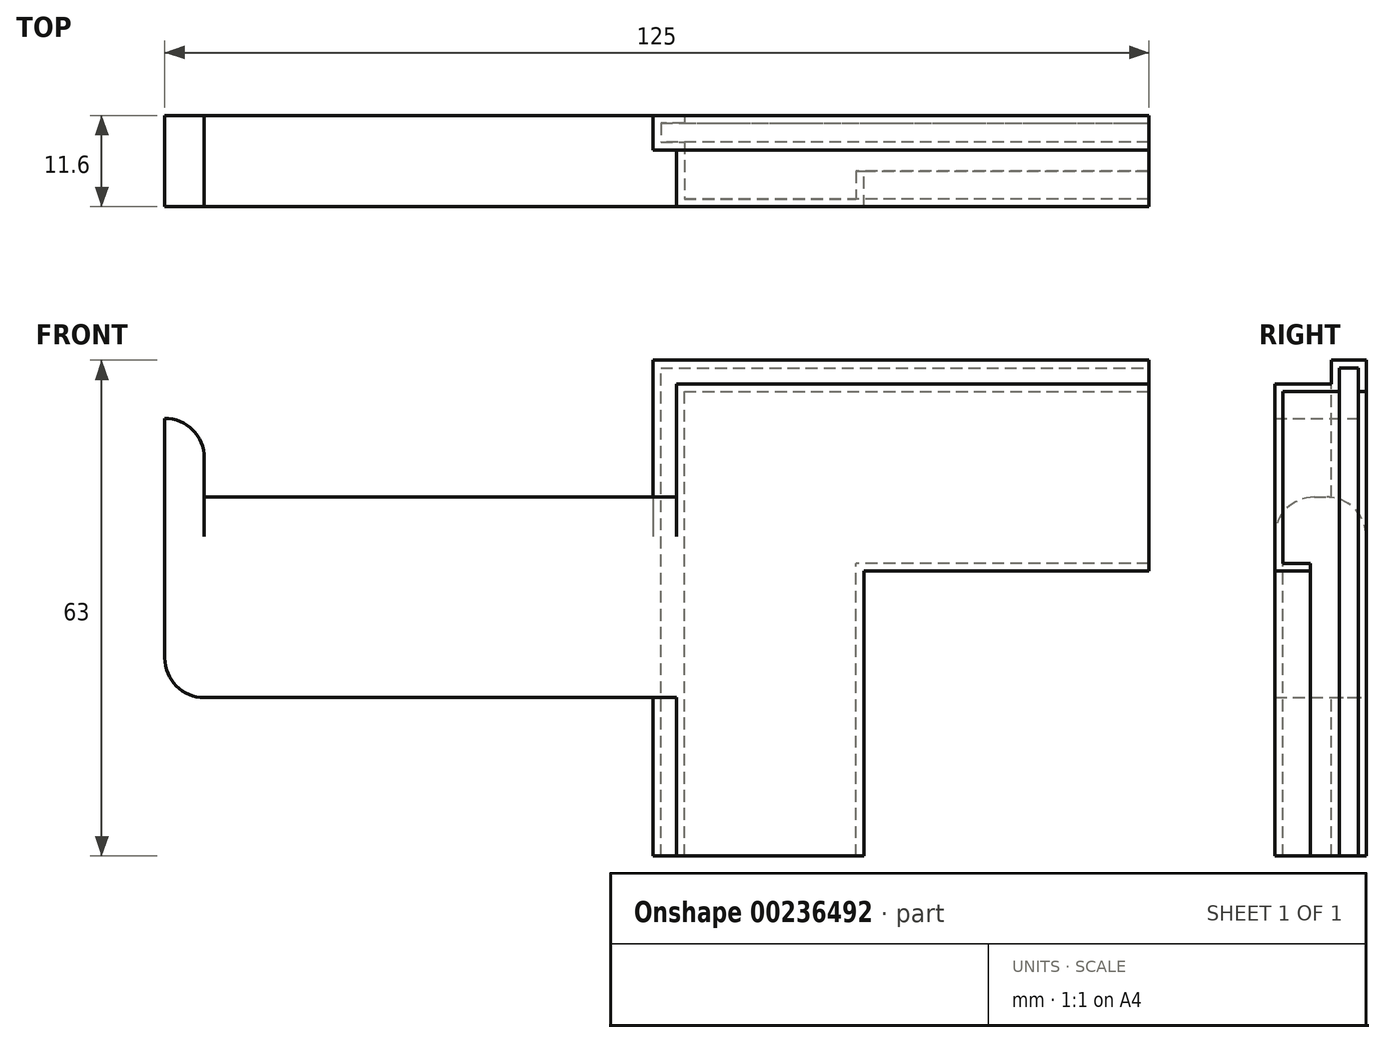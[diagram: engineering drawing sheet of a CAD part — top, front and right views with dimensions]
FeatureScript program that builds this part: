
annotation { "Feature Type Name" : "Feature", "Feature Type Description" : "" }
export const myFeature = defineFeature(function(context is Context, id is Id, definition is map)
    precondition{}
    {
        {
            var Q0;
            Q0=qCreatedBy(makeId("Front.planeOp"),FACE);
            var sketch = newSketch(context, id + "F0", { "sketchPlane" : qUnion([Q0])});
            skLineSegment(sketch, "E0.bottom", {"start": v(-30, 30) * mm, "end": v(30, 30) * mm});
            skLineSegment(sketch, "E0.top", {"start": v(-30, 6.2) * mm, "end": v(30, 6.2) * mm});
            skLineSegment(sketch, "E0.left", {"start": v(-30, 30) * mm, "end": v(-30, 6.2) * mm});
            skLineSegment(sketch, "E0.right", {"start": v(30, 30) * mm, "end": v(30, 6.2) * mm});
            skLineSegment(sketch, "E1.bottom", {"start": v(-30, 30) * mm, "end": v(-6.2, 30) * mm});
            skLineSegment(sketch, "E1.top", {"start": v(-30, -30) * mm, "end": v(-6.2, -30) * mm});
            skLineSegment(sketch, "E1.left", {"start": v(-30, 30) * mm, "end": v(-30, -30) * mm});
            skLineSegment(sketch, "E1.right", {"start": v(-6.2, 30) * mm, "end": v(-6.2, -30) * mm});
            skSolve(sketch);
        }
        {
            var Q0;
            Q0 = qSketchRegion(id + "F0", true);
            extrude(context, id + "F1", {"entities" : qUnion([Q0]), "depth" : 1 * mm});
        }
        {
            var Q0;
            Q0=makeQuery(id+"F1.opExtrude","CAP_FACE",FACE,{"disambiguationData":[OSD([sQuery(id+"F0.wireOp",EDGE,"E0.bottom"),sQuery(id+"F0.wireOp",EDGE,"E0.top"),sQuery(id+"F0.wireOp",EDGE,"E0.right"),sQuery(id+"F0.wireOp",EDGE,"E1.bottom"),sQuery(id+"F0.wireOp",EDGE,"E1.top"),sQuery(id+"F0.wireOp",EDGE,"E1.left"),sQuery(id+"F0.wireOp",EDGE,"E1.right")])],"isStart":true});
            var sketch = newSketch(context, id + "F2", { "sketchPlane" : qUnion([Q0])});
            skLineSegment(sketch, "E2.bottom", {"start": v(-30, 30) * mm, "end": v(30, 30) * mm});
            skLineSegment(sketch, "E2.top", {"start": v(-30, 29) * mm, "end": v(30, 29) * mm});
            skLineSegment(sketch, "E2.left", {"start": v(-30, 30) * mm, "end": v(-30, 29) * mm});
            skLineSegment(sketch, "E2.right", {"start": v(30, 30) * mm, "end": v(30, 29) * mm});
            skLineSegment(sketch, "E3.bottom", {"start": v(30, 30) * mm, "end": v(29, 30) * mm});
            skLineSegment(sketch, "E3.top", {"start": v(30, -30) * mm, "end": v(29, -30) * mm});
            skLineSegment(sketch, "E3.left", {"start": v(30, 30) * mm, "end": v(30, -30) * mm});
            skLineSegment(sketch, "E3.right", {"start": v(29, 30) * mm, "end": v(29, -30) * mm});
            skSolve(sketch);
        }
        {
            var Q0;
            Q0 = qSketchRegion(id + "F2", true);
            extrude(context, id + "F3", {"entities" : qUnion([Q0]), "operationType" : NewBodyOperationType.ADD, "depth" : 7.2 * mm});
        }
        {
            var Q0;
            Q0=makeQuery(id+"F1.opExtrude","CAP_FACE",FACE,{"disambiguationData":[OSD([sQuery(id+"F0.wireOp",EDGE,"E0.bottom"),sQuery(id+"F0.wireOp",EDGE,"E0.top"),sQuery(id+"F0.wireOp",EDGE,"E0.right"),sQuery(id+"F0.wireOp",EDGE,"E1.bottom"),sQuery(id+"F0.wireOp",EDGE,"E1.top"),sQuery(id+"F0.wireOp",EDGE,"E1.left"),sQuery(id+"F0.wireOp",EDGE,"E1.right")])],"isStart":true});
            var sketch = newSketch(context, id + "F4", { "sketchPlane" : qUnion([Q0])});
            skLineSegment(sketch, "E4.bottom", {"start": v(-30, 6.2) * mm, "end": v(6.2, 6.2) * mm});
            skLineSegment(sketch, "E4.top", {"start": v(-30, 7.2) * mm, "end": v(6.2, 7.2) * mm});
            skLineSegment(sketch, "E4.left", {"start": v(-30, 6.2) * mm, "end": v(-30, 7.2) * mm});
            skLineSegment(sketch, "E4.right", {"start": v(6.2, 6.2) * mm, "end": v(6.2, 7.2) * mm});
            skLineSegment(sketch, "E5.bottom", {"start": v(6.2, -30) * mm, "end": v(7.2, -30) * mm});
            skLineSegment(sketch, "E5.top", {"start": v(6.2, 7.2) * mm, "end": v(7.2, 7.2) * mm});
            skLineSegment(sketch, "E5.left", {"start": v(6.2, -30) * mm, "end": v(6.2, 7.2) * mm});
            skLineSegment(sketch, "E5.right", {"start": v(7.2, -30) * mm, "end": v(7.2, 7.2) * mm});
            skSolve(sketch);
        }
        {
            var Q0;
            Q0 = qSketchRegion(id + "F4", true);
            extrude(context, id + "F5", {"entities" : qUnion([Q0]), "operationType" : NewBodyOperationType.ADD, "depth" : 3.5 * mm});
        }
        {
            var Q0;
            Q0=makeQuery(id+"F3.boolean.opBoolean","MERGE",FACE,{"derivedFrom":[makeQuery(id+"F1.opExtrude","SWEPT_FACE",FACE,{"disambiguationData":[OSD([sQuery(id+"F0.wireOp",EDGE,"E0.bottom"),sQuery(id+"F0.wireOp",EDGE,"E1.bottom")])]}),makeQuery(id+"F3.opExtrude","SWEPT_FACE",FACE,{"disambiguationData":[OSD([sQuery(id+"F2.wireOp",EDGE,"E2.bottom"),sQuery(id+"F2.wireOp",EDGE,"E3.bottom")])]})]});
            var sketch = newSketch(context, id + "F6", { "sketchPlane" : qUnion([Q0])});
            skLineSegment(sketch, "E6.bottom", {"start": v(-30, 7.2) * mm, "end": v(30, 7.2) * mm});
            skLineSegment(sketch, "E6.top", {"start": v(-30, 6.2) * mm, "end": v(30, 6.2) * mm});
            skLineSegment(sketch, "E6.left", {"start": v(-30, 7.2) * mm, "end": v(-30, 6.2) * mm});
            skLineSegment(sketch, "E6.right", {"start": v(30, 7.2) * mm, "end": v(30, 6.2) * mm});
            skSolve(sketch);
        }
        {
            var Q0;
            Q0 = qSketchRegion(id + "F6", true);
            extrude(context, id + "F7", {"entities" : qUnion([Q0]), "operationType" : NewBodyOperationType.ADD, "depth" : 3 * mm});
        }
        {
            var Q0;
            Q0=makeQuery(id+"F7.boolean.opBoolean","MERGE",FACE,{"derivedFrom":[makeQuery(id+"F3.opExtrude","CAP_FACE",FACE,{"disambiguationData":[OSD([sQuery(id+"F2.wireOp",EDGE,"E2.bottom"),sQuery(id+"F2.wireOp",EDGE,"E2.top"),sQuery(id+"F2.wireOp",EDGE,"E2.left"),sQuery(id+"F2.wireOp",EDGE,"E3.bottom"),sQuery(id+"F2.wireOp",EDGE,"E3.top"),sQuery(id+"F2.wireOp",EDGE,"E3.left"),sQuery(id+"F2.wireOp",EDGE,"E3.right")])],"isStart":false}),makeQuery(id+"F7.opExtrude","SWEPT_FACE",FACE,{"disambiguationData":[OSD([sQuery(id+"F6.wireOp",EDGE,"E6.bottom")])]})]});
            var sketch = newSketch(context, id + "F8", { "sketchPlane" : qUnion([Q0])});
            skLineSegment(sketch, "E7.bottom", {"start": v(-30, 33) * mm, "end": v(30, 33) * mm});
            skLineSegment(sketch, "E7.top", {"start": v(-30, 32) * mm, "end": v(30, 32) * mm});
            skLineSegment(sketch, "E7.left", {"start": v(-30, 33) * mm, "end": v(-30, 32) * mm});
            skLineSegment(sketch, "E7.right", {"start": v(30, 33) * mm, "end": v(30, 32) * mm});
            skSolve(sketch);
        }
        {
            var Q0;
            Q0 = qSketchRegion(id + "F8", true);
            extrude(context, id + "F9", {"entities" : qUnion([Q0]), "operationType" : NewBodyOperationType.ADD, "depth" : 3.4 * mm});
        }
        {
            var Q0;
            Q0=makeQuery(id+"F9.opExtrude","SWEPT_FACE",FACE,{"disambiguationData":[OSD([sQuery(id+"F8.wireOp",EDGE,"E7.top")])]});
            var sketch = newSketch(context, id + "F10", { "sketchPlane" : qUnion([Q0])});
            skLineSegment(sketch, "E8.bottom", {"start": v(-30, -10.6) * mm, "end": v(30, -10.6) * mm});
            skLineSegment(sketch, "E8.top", {"start": v(-30, -9.6) * mm, "end": v(30, -9.6) * mm});
            skLineSegment(sketch, "E8.left", {"start": v(-30, -10.6) * mm, "end": v(-30, -9.6) * mm});
            skLineSegment(sketch, "E8.right", {"start": v(30, -10.6) * mm, "end": v(30, -9.6) * mm});
            skSolve(sketch);
        }
        {
            var Q0;
            Q0 = qSketchRegion(id + "F10", true);
            extrude(context, id + "F11", {"entities" : qUnion([Q0]), "operationType" : NewBodyOperationType.ADD, "depth" : 3 * mm});
        }
        {
            var Q0;
            Q0=makeQuery(id+"F11.boolean.opBoolean","MERGE",FACE,{"derivedFrom":[makeQuery(id+"F9.boolean.opBoolean","MERGE",FACE,{"derivedFrom":[makeQuery(id+"F7.boolean.opBoolean","MERGE",FACE,{"derivedFrom":[makeQuery(id+"F3.boolean.opBoolean","MERGE",FACE,{"derivedFrom":[makeQuery(id+"F1.opExtrude","SWEPT_FACE",FACE,{"disambiguationData":[OSD([sQuery(id+"F0.wireOp",EDGE,"E1.left")])]}),makeQuery(id+"F3.opExtrude","SWEPT_FACE",FACE,{"disambiguationData":[OSD([sQuery(id+"F2.wireOp",EDGE,"E3.left")])]})]}),makeQuery(id+"F7.opExtrude","SWEPT_FACE",FACE,{"disambiguationData":[OSD([sQuery(id+"F6.wireOp",EDGE,"E6.left")])]})]}),makeQuery(id+"F9.opExtrude","SWEPT_FACE",FACE,{"disambiguationData":[OSD([sQuery(id+"F8.wireOp",EDGE,"E7.right")])]})]}),makeQuery(id+"F11.opExtrude","SWEPT_FACE",FACE,{"disambiguationData":[OSD([sQuery(id+"F10.wireOp",EDGE,"E8.left")])]})]});
            var sketch = newSketch(context, id + "F12", { "sketchPlane" : qUnion([Q0])});
            skLineSegment(sketch, "E9.bottom", {"start": v(-7.2, -30) * mm, "end": v(-6.2, -30) * mm});
            skLineSegment(sketch, "E9.top", {"start": v(-7.2, 30) * mm, "end": v(-6.2, 30) * mm});
            skLineSegment(sketch, "E9.left", {"start": v(-7.2, -30) * mm, "end": v(-7.2, 30) * mm});
            skLineSegment(sketch, "E9.right", {"start": v(-6.2, -30) * mm, "end": v(-6.2, 30) * mm});
            skSolve(sketch);
        }
        {
            var Q0;
            Q0 = qSketchRegion(id + "F12", true);
            extrude(context, id + "F13", {"entities" : qUnion([Q0]), "operationType" : NewBodyOperationType.ADD, "depth" : 3 * mm});
        }
        {
            var Q0;
            Q0=makeQuery(id+"F13.boolean.opBoolean","MERGE",FACE,{"derivedFrom":[makeQuery(id+"F7.boolean.opBoolean","MERGE",FACE,{"derivedFrom":[makeQuery(id+"F3.opExtrude","CAP_FACE",FACE,{"disambiguationData":[OSD([sQuery(id+"F2.wireOp",EDGE,"E2.bottom"),sQuery(id+"F2.wireOp",EDGE,"E2.top"),sQuery(id+"F2.wireOp",EDGE,"E2.left"),sQuery(id+"F2.wireOp",EDGE,"E3.bottom"),sQuery(id+"F2.wireOp",EDGE,"E3.top"),sQuery(id+"F2.wireOp",EDGE,"E3.left"),sQuery(id+"F2.wireOp",EDGE,"E3.right")])],"isStart":false}),makeQuery(id+"F7.opExtrude","SWEPT_FACE",FACE,{"disambiguationData":[OSD([sQuery(id+"F6.wireOp",EDGE,"E6.bottom")])]})]}),makeQuery(id+"F13.opExtrude","SWEPT_FACE",FACE,{"disambiguationData":[OSD([sQuery(id+"F12.wireOp",EDGE,"E9.left")])]})]});
            var sketch = newSketch(context, id + "F14", { "sketchPlane" : qUnion([Q0])});
            skLineSegment(sketch, "E10.bottom", {"start": v(33, -30) * mm, "end": v(32, -30) * mm});
            skLineSegment(sketch, "E10.top", {"start": v(33, 30) * mm, "end": v(32, 30) * mm});
            skLineSegment(sketch, "E10.left", {"start": v(33, -30) * mm, "end": v(33, 30) * mm});
            skLineSegment(sketch, "E10.right", {"start": v(32, -30) * mm, "end": v(32, 30) * mm});
            skSolve(sketch);
        }
        {
            var Q0;
            Q0 = qSketchRegion(id + "F14", true);
            extrude(context, id + "F15", {"entities" : qUnion([Q0]), "operationType" : NewBodyOperationType.ADD, "depth" : 3.4 * mm});
        }
        {
            var Q0;
            Q0=makeQuery(id+"F15.opExtrude","SWEPT_FACE",FACE,{"disambiguationData":[OSD([sQuery(id+"F14.wireOp",EDGE,"E10.right")])]});
            var sketch = newSketch(context, id + "F16", { "sketchPlane" : qUnion([Q0])});
            skLineSegment(sketch, "E11.bottom", {"start": v(10.6, -30) * mm, "end": v(9.6, -30) * mm});
            skLineSegment(sketch, "E11.top", {"start": v(10.6, 30) * mm, "end": v(9.6, 30) * mm});
            skLineSegment(sketch, "E11.left", {"start": v(10.6, -30) * mm, "end": v(10.6, 30) * mm});
            skLineSegment(sketch, "E11.right", {"start": v(9.6, -30) * mm, "end": v(9.6, 30) * mm});
            skSolve(sketch);
        }
        {
            var Q0;
            Q0 = qSketchRegion(id + "F16", true);
            extrude(context, id + "F17", {"entities" : qUnion([Q0]), "operationType" : NewBodyOperationType.ADD, "depth" : 3 * mm});
        }
        {
            var Q0;
            {var subQ1=sQuery(id+"F2.wireOp",EDGE,"E3.left");var subQ4=sQuery(id+"F6.wireOp",EDGE,"E6.left");var subQ5=sQuery(id+"F6.wireOp",EDGE,"E6.bottom");var subQ6=makeQuery(id+"F3.opExtrude","SWEPT_FACE",FACE,{"disambiguationData":[OSD([subQ1])]});var subQ7=sQuery(id+"F10.wireOp",EDGE,"E8.left");var subQ8=makeQuery(id+"F11.opExtrude","SWEPT_FACE",FACE,{"disambiguationData":[OSD([subQ7])]});var subQ9=makeQuery(id+"F1.opExtrude","SWEPT_FACE",FACE,{"disambiguationData":[OSD([sQuery(id+"F0.wireOp",EDGE,"E1.left")])]});var subQ12=makeQuery(id+"F7.opExtrude","SWEPT_FACE",FACE,{"disambiguationData":[OSD([subQ4])]});var subQ13=sQuery(id+"F8.wireOp",EDGE,"E7.right");var subQ14=makeQuery(id+"F9.opExtrude","SWEPT_FACE",FACE,{"disambiguationData":[OSD([subQ13])]});Q0=makeQuery(id+"F13.boolean.opBoolean","SPLIT",FACE,{"disambiguationData":[TD([makeQuery(id+"F7.opExtrude","SWEPT_FACE",FACE,{"disambiguationData":[OSD([subQ5])]})])],"derivedFrom":makeQuery(id+"F11.boolean.opBoolean","MERGE",FACE,{"derivedFrom":[makeQuery(id+"F9.boolean.opBoolean","MERGE",FACE,{"derivedFrom":[makeQuery(id+"F7.boolean.opBoolean","MERGE",FACE,{"derivedFrom":[makeQuery(id+"F3.boolean.opBoolean","MERGE",FACE,{"derivedFrom":[subQ9,subQ6]}),subQ12]}),subQ14]}),subQ8]})});}
            extrude(context, id + "F18", {"entities" : qUnion([Q0]), "operationType" : NewBodyOperationType.ADD, "depth" : 3 * mm});
        }
        {
            var Q0;
            Q0=makeQuery(id+"F17.boolean.opBoolean","MERGE",FACE,{"derivedFrom":[makeQuery(id+"F15.boolean.opBoolean","MERGE",FACE,{"derivedFrom":[makeQuery(id+"F13.opExtrude","SWEPT_FACE",FACE,{"disambiguationData":[OSD([sQuery(id+"F12.wireOp",EDGE,"E9.top")])]}),makeQuery(id+"F15.opExtrude","SWEPT_FACE",FACE,{"disambiguationData":[OSD([sQuery(id+"F14.wireOp",EDGE,"E10.top")])]})]}),makeQuery(id+"F17.opExtrude","SWEPT_FACE",FACE,{"disambiguationData":[OSD([sQuery(id+"F16.wireOp",EDGE,"E11.top")])]})]});
            extrude(context, id + "F19", {"entities" : qUnion([Q0]), "operationType" : NewBodyOperationType.ADD, "depth" : 2 * mm});
        }
        {
            var Q0;
            {var subQ2=makeQuery(id+"F3.opExtrude","SWEPT_FACE",FACE,{"disambiguationData":[OSD([sQuery(id+"F2.wireOp",EDGE,"E3.left")])]});var subQ3=sQuery(id+"F0.wireOp",EDGE,"E1.left");var subQ4=sQuery(id+"F0.wireOp",EDGE,"E1.top");var subQ5=makeQuery(id+"F11.opExtrude","SWEPT_FACE",FACE,{"disambiguationData":[OSD([sQuery(id+"F10.wireOp",EDGE,"E8.left")])]});var subQ6=makeQuery(id+"F7.opExtrude","SWEPT_FACE",FACE,{"disambiguationData":[OSD([sQuery(id+"F6.wireOp",EDGE,"E6.left")])]});var subQ7=makeQuery(id+"F9.opExtrude","SWEPT_FACE",FACE,{"disambiguationData":[OSD([sQuery(id+"F8.wireOp",EDGE,"E7.right")])]});var subQ8=makeQuery(id+"F1.opExtrude","SWEPT_FACE",FACE,{"disambiguationData":[OSD([subQ3])]});Q0=makeQuery(id+"F13.boolean.opBoolean","SPLIT",FACE,{"disambiguationData":[TD([makeQuery(id+"F1.opExtrude","SWEPT_FACE",FACE,{"disambiguationData":[OSD([subQ4])]})])],"derivedFrom":makeQuery(id+"F11.boolean.opBoolean","MERGE",FACE,{"derivedFrom":[makeQuery(id+"F9.boolean.opBoolean","MERGE",FACE,{"derivedFrom":[makeQuery(id+"F7.boolean.opBoolean","MERGE",FACE,{"derivedFrom":[makeQuery(id+"F3.boolean.opBoolean","MERGE",FACE,{"derivedFrom":[subQ8,subQ2]}),subQ6]}),subQ7]}),subQ5]})});}
            var sketch = newSketch(context, id + "F20", { "sketchPlane" : qUnion([Q0])});
            skLineSegment(sketch, "E12.bottom", {"start": v(1, 15.6) * mm, "end": v(-6.2, 15.6) * mm});
            skLineSegment(sketch, "E12.top", {"start": v(1, -9.85) * mm, "end": v(-6.2, -9.85) * mm});
            skLineSegment(sketch, "E12.left", {"start": v(1, 15.6) * mm, "end": v(1, -9.85) * mm});
            skLineSegment(sketch, "E12.right", {"start": v(-6.2, 15.6) * mm, "end": v(-6.2, -9.85) * mm});
            skSolve(sketch);
        }
        {
            var Q0;
            Q0 = qSketchRegion(id + "F20", true);
            extrude(context, id + "F21", {"entities" : qUnion([Q0]), "operationType" : NewBodyOperationType.ADD, "depth" : 65 * mm});
        }
        {
            var Q0;
            {var subQ0=sQuery(id+"F14.wireOp",EDGE,"E10.left");var subQ1=sQuery(id+"F12.wireOp",EDGE,"E9.top");Q0=makeQuery(id+"F19.boolean.opBoolean","MERGE",FACE,{"derivedFrom":[makeQuery(id+"F18.boolean.opBoolean","MERGE",FACE,{"derivedFrom":[makeQuery(id+"F15.boolean.opBoolean","MERGE",FACE,{"derivedFrom":[makeQuery(id+"F13.opExtrude","CAP_FACE",FACE,{"disambiguationData":[OSD([sQuery(id+"F12.wireOp",EDGE,"E9.bottom"),subQ1,sQuery(id+"F12.wireOp",EDGE,"E9.left"),sQuery(id+"F12.wireOp",EDGE,"E9.right")])],"isStart":false}),makeQuery(id+"F15.opExtrude","SWEPT_FACE",FACE,{"disambiguationData":[OSD([subQ0])]})]}),makeQuery(id+"F18.opExtrude","CAP_FACE",FACE,{"disambiguationData":[OSD([sQuery(id+"F0.wireOp",EDGE,"E1.left"),sQuery(id+"F2.wireOp",EDGE,"E3.left"),sQuery(id+"F6.wireOp",EDGE,"E6.left"),sQuery(id+"F8.wireOp",EDGE,"E7.right"),sQuery(id+"F10.wireOp",EDGE,"E8.left")])],"isStart":false})]}),makeQuery(id+"F19.opExtrude","SWEPT_FACE",FACE,{"disambiguationData":[OSD([subQ1,sQuery(id+"F14.wireOp",EDGE,"E10.top"),subQ0])]})]});}
            var sketch = newSketch(context, id + "F22", { "sketchPlane" : qUnion([Q0])});
            skLineSegment(sketch, "E13.bottom", {"start": v(-6.2, 15.6) * mm, "end": v(-10.6, 15.6) * mm});
            skLineSegment(sketch, "E13.top", {"start": v(-6.2, -9.85) * mm, "end": v(-10.6, -9.85) * mm});
            skLineSegment(sketch, "E13.left", {"start": v(-6.2, 15.6) * mm, "end": v(-6.2, -9.85) * mm});
            skLineSegment(sketch, "E13.right", {"start": v(-10.6, 15.6) * mm, "end": v(-10.6, -9.85) * mm});
            skSolve(sketch);
        }
        {
            var Q0;
            Q0 = qSketchRegion(id + "F22", true);
            extrude(context, id + "F23", {"entities" : qUnion([Q0]), "operationType" : NewBodyOperationType.ADD, "depth" : 62 * mm});
        }
        {
            var Q0;
            Q0=makeQuery(id+"F23.boolean.opBoolean","MERGE",FACE,{"derivedFrom":[makeQuery(id+"F21.opExtrude","SWEPT_FACE",FACE,{"disambiguationData":[OSD([sQuery(id+"F20.wireOp",EDGE,"E12.bottom")])]}),makeQuery(id+"F23.opExtrude","SWEPT_FACE",FACE,{"disambiguationData":[OSD([sQuery(id+"F22.wireOp",EDGE,"E13.bottom")])]})]});
            var sketch = newSketch(context, id + "F24", { "sketchPlane" : qUnion([Q0])});
            skLineSegment(sketch, "E14.bottom", {"start": v(-95, 10.6) * mm, "end": v(-90, 10.6) * mm});
            skLineSegment(sketch, "E14.top", {"start": v(-95, -1) * mm, "end": v(-90, -1) * mm});
            skLineSegment(sketch, "E14.left", {"start": v(-95, 10.6) * mm, "end": v(-95, -1) * mm});
            skLineSegment(sketch, "E14.right", {"start": v(-90, 10.6) * mm, "end": v(-90, -1) * mm});
            skSolve(sketch);
        }
        {
            var Q0;
            Q0 = qSketchRegion(id + "F24", true);
            extrude(context, id + "F25", {"entities" : qUnion([Q0]), "operationType" : NewBodyOperationType.ADD, "depth" : 10 * mm});
        }
        {
            var Q0;
            Q0=makeQuery(id+"F25.opExtrude","CAP_EDGE",EDGE,{"disambiguationData":[OSD([sQuery(id+"F24.wireOp",EDGE,"E14.right")])],"isStart":false});
            fillet(context, id + "F26", {"entities" : qUnion([Q0]), "radius" : 5 * mm, "tangentPropagation" : true, "allowEdgeOverflow" : false});
        }
        {
            var Q0;
            Q0=makeQuery(id+"F21.opExtrude","SWEPT_EDGE",EDGE,{"disambiguationData":[OSD([sQuery(id+"F0.wireOp",EDGE,"E1.left"),sQuery(id+"F20.wireOp",EDGE,"E12.bottom"),sQuery(id+"F20.wireOp",EDGE,"E12.left")])]});
            var Q1;
            Q1=makeQuery(id+"F23.opExtrude","SWEPT_EDGE",EDGE,{"disambiguationData":[OSD([sQuery(id+"F8.wireOp",EDGE,"E7.right"),sQuery(id+"F10.wireOp",EDGE,"E8.bottom"),sQuery(id+"F10.wireOp",EDGE,"E8.left"),sQuery(id+"F14.wireOp",EDGE,"E10.left"),sQuery(id+"F22.wireOp",EDGE,"E13.bottom"),sQuery(id+"F22.wireOp",EDGE,"E13.right")])]});
            fillet(context, id + "F27", {"entities" : qUnion([Q0, Q1]), "radius" : 5 * mm, "tangentPropagation" : true, "allowEdgeOverflow" : false});
        }
        {
            var Q0;
            Q0=makeQuery(id+"F23.boolean.opBoolean","MERGE",EDGE,{"derivedFrom":[makeQuery(id+"F21.opExtrude","CAP_EDGE",EDGE,{"disambiguationData":[OSD([sQuery(id+"F20.wireOp",EDGE,"E12.top")])],"isStart":false}),makeQuery(id+"F23.opExtrude","CAP_EDGE",EDGE,{"disambiguationData":[OSD([sQuery(id+"F22.wireOp",EDGE,"E13.top")])],"isStart":false})]});
            fillet(context, id + "F28", {"entities" : qUnion([Q0]), "radius" : 5 * mm, "tangentPropagation" : true, "allowEdgeOverflow" : false});
        }
    });
